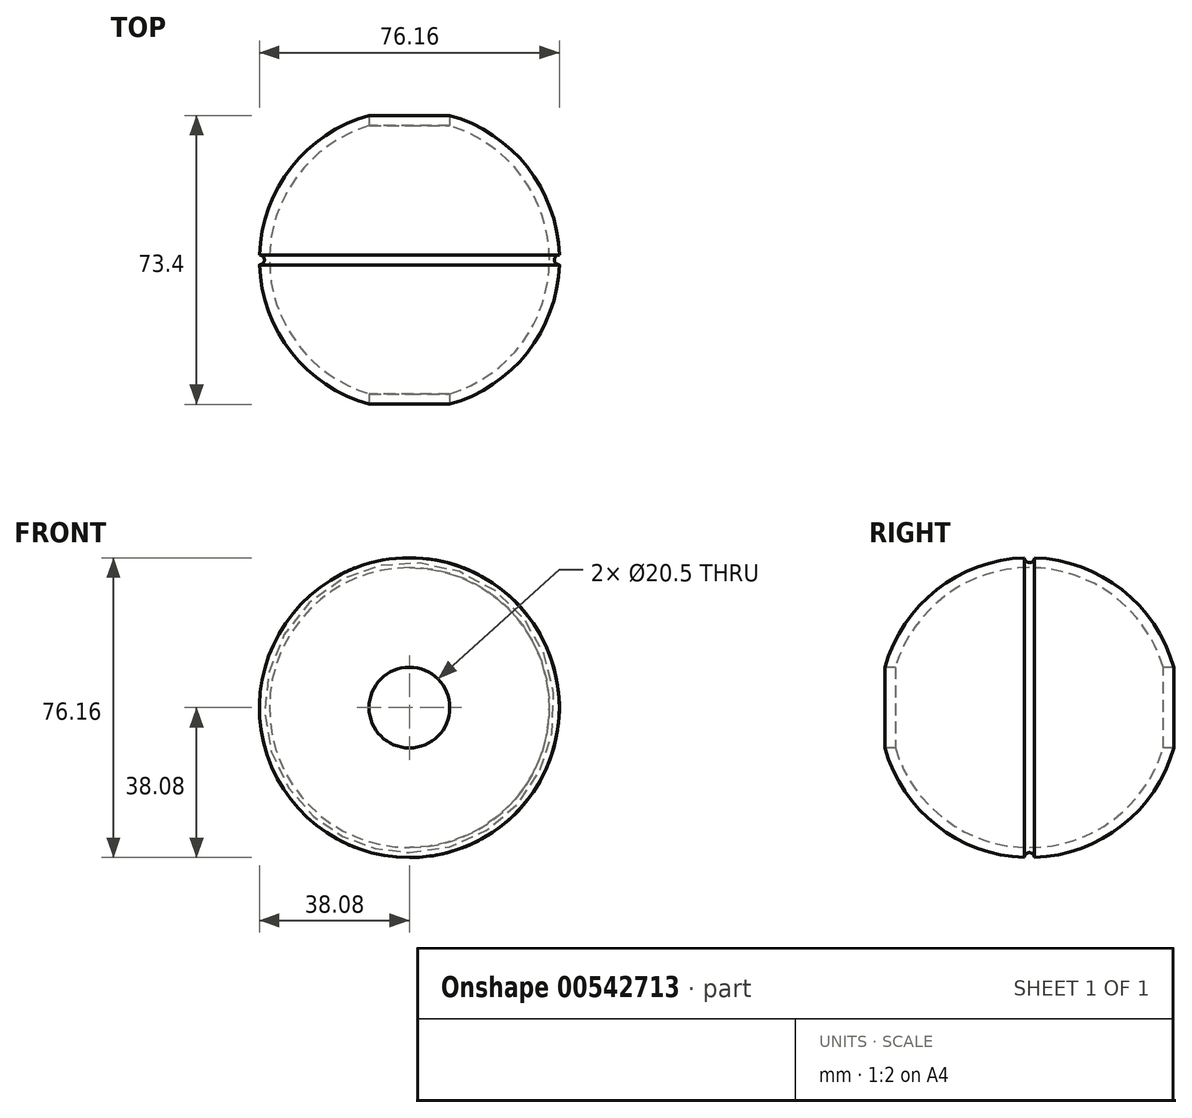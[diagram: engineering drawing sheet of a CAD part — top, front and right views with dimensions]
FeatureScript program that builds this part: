
annotation { "Feature Type Name" : "Feature", "Feature Type Description" : "" }
export const myFeature = defineFeature(function(context is Context, id is Id, definition is map)
    precondition{}
    {
        {
            var Q0;
            Q0=qCreatedBy(makeId("Front.planeOp"),FACE);
            var sketch = newSketch(context, id + "F0", { "sketchPlane" : qUnion([Q0])});
            skLineSegment(sketch, "E0", {"start": v(0, 35.56) * mm, "end": v(0, 38.1) * mm});
            skArc(sketch, "E1", {"start": v(0, 38.1) * mm, "mid": v(-38.1, 0) * mm, "end": v(0, -38.1) * mm});
            skLineSegment(sketch, "E2", {"start": v(0, -35.56) * mm, "end": v(0, -38.1) * mm});
            skArc(sketch, "E3", {"start": v(0, 35.56) * mm, "mid": v(-35.56, 0) * mm, "end": v(0, -35.56) * mm});
            skSolve(sketch);
        }
        {
            var Q0;
            Q0 = qSketchRegion(id + "F0", true);
            var Q1;
            Q1=sQuery(id+"F0.wireOp",EDGE,"E0");
            revolve(context, id + "F1", {"entities" : qUnion([Q0]), "axis" : qUnion([Q1]), "revolveType" : RevolveType.FULL});
        }
        {
            var Q0;
            Q0=qCreatedBy(makeId("Front.planeOp"),FACE);
            var sketch = newSketch(context, id + "F2", { "sketchPlane" : qUnion([Q0])});
            skCircle(sketch, "E4", {"center": v(0, 0) * mm, "radius": 10.25 * mm});
            skSolve(sketch);
        }
        {
            var Q0;
            Q0 = qSketchRegion(id + "F2", true);
            extrude(context, id + "F3", {"entities" : qUnion([Q0]), "operationType" : NewBodyOperationType.REMOVE, "endBound" : BoundingType.SYMMETRIC, "oppositeDirection" : true, "depth" : 242.82 * mm, "offsetDistance" : 25.4 * mm});
        }
        {
            var Q0;
            Q0=qCreatedBy(makeId("Front.planeOp"),FACE);
            var sketch = newSketch(context, id + "F4", { "sketchPlane" : qUnion([Q0])});
            skLineSegment(sketch, "E5", {"start": v(0, 0) * mm, "end": v(68.2, 0) * mm});
            skLineSegment(sketch, "E6", {"start": v(0, 0) * mm, "end": v(-39.94, 39.94) * mm});
            skLineSegment(sketch, "E7", {"start": v(0, 0) * mm, "end": v(42.45, 42.45) * mm});
            skSolve(sketch);
        }
        {
            var Q0;
            Q0=qCreatedBy(makeId("Front.planeOp"),FACE);
            var sketch = newSketch(context, id + "F5", { "sketchPlane" : qUnion([Q0])});
            skCircle(sketch, "E8", {"center": v(0, 0) * mm, "radius": 38.1 * mm});
            skSolve(sketch);
        }
        {
            var Q0;
            Q0=qCreatedBy(makeId("Right.planeOp"),FACE);
            var sketch = newSketch(context, id + "F6", { "sketchPlane" : qUnion([Q0])});
            skCircle(sketch, "E9", {"center": v(0, 38.1) * mm, "radius": 1.27 * mm});
            skSolve(sketch);
        }
        {
            var Q0;
            Q0=makeQuery(id+"F6.imprint","IMPRINT",FACE,{"disambiguationData":[TD([[makeQuery(id+"F6.imprint","IMPRINT",EDGE,{"derivedFrom":sQuery(id+"F6.wireOp",EDGE,"E9")}),1.0]])]});
            var Q1;
            Q1=sQuery(id+"F5.wireOp",EDGE,"E8");
            sweep(context, id + "F7", {"operationType" : NewBodyOperationType.REMOVE, "profiles" : qUnion([Q0]), "path" : qUnion([Q1])});
        }
    });
